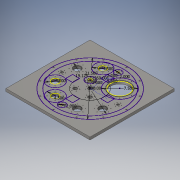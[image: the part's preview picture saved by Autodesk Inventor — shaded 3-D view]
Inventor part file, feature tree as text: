
AUTODESK INVENTOR PART (.ipt)
format: ipt  version: 2018 (Build 220112000, 112)  size: 472,064 bytes
history: native  units: in
note: dims shown in document units (in); Inventor stores cm internally (conversion verified against a paired STEP export)
features: sketch x23, extrude x13, hole x7, pattern_circular x5
ambient origin geometry x8: Origin, YZ Plane, XZ Plane, XY Plane, X Axis, Y Axis, Z Axis, Center Point
bodies: Solid1 (feature_tree)
feature tree (48):
  extrude  "Extrusion1"  Depth=24.0in
  sketch  "Sketch23"  dims[d26=0.1in d27=0.0in]
  extrude  "Extrusion2"  Depth=0.75in
  hole  "Hole1"  [1 undecoded]
  extrude  "Extrusion3"  Depth=1.0in TaperAngle=0.0deg
  extrude  "Extrusion4"  TaperAngle=0.0deg  [1 undecoded]
  hole  "Hole2"  [1 undecoded]
  pattern_circular  "Circular Pattern1"  Count=8 Angle=360.0deg
  extrude  "Extrusion5"  Depth=0.25in
  extrude  "Extrusion6"  Depth=1.04in
  hole  "Hole3"  [1 undecoded]
  pattern_circular  "Circular Pattern5"  Count=6 Angle=360.0deg
  extrude  "Extrusion16"  Depth=0.25in TaperAngle=180.0deg
  extrude  "Extrusion17"  Depth=19.125in
  hole  "Hole9"  [1 undecoded]
  pattern_circular  "Circular Pattern6"  Angle=270.0deg  [1 undecoded]
  sketch  "Sketch29"  dims[d37=0.156in d38=0.38in d39=0.375in d40=0.25in d41=0.5635in d42=0.536in d43=0.8108in d44=3.0in]
  extrude  "Extrusion18"  Depth=0.125in
  extrude  "Extrusion19"  Depth=0.1in TaperAngle=0.0deg
  hole  "Hole10"  [1 undecoded]
  sketch  "Sketch25"  dims[d28=1.9in]
  pattern_circular  "Circular Pattern7"  [2 undecoded]
  extrude  "Extrusion20"  Depth=0.75in
  extrude  "Extrusion21"  TaperAngle=180.0deg  [1 undecoded]
  hole  "Hole11"  [1 undecoded]
  hole  "Hole13"  [1 undecoded]
  pattern_circular  "Circular Pattern9"  [2 undecoded]
  extrude  "Extrusion22"  Depth=0.125in
  sketch  "Sketch1"  dims[d0=24.0in d1=24.0in]
  sketch  "Sketch2"  dims[d2=0.75in d3=0.0in d4=6.0in]
  sketch  "Sketch3"  dims[d5=45.0deg d6=9.35in]
  sketch  "Sketch4"  dims[d7=5.25in d8=1.0in d9=0.0in]
  sketch  "Sketch5"  dims[d10=3.4in d11=0.0in]
  sketch  "Sketch6"  dims[d12=3.1496in d14=360.0deg]
  sketch  "Sketch7"  dims[d16=0.196in d17=0.4in d18=0.375in d19=0.25in d20=0.5635in d21=0.6in d22=0.8108in d23=7.5in]
  sketch  "Sketch8"  dims[d24=1.4086in]
  sketch  "Sketch9"  dims[d25=2.07in]
  sketch  "Sketch26"  dims[d29=0.1in d30=0.0in]
  sketch  "Sketch27"  dims[d31=1.625in]
  sketch  "Sketch28"  dims[d32=0.0in d33=3.1496in d35=360.0deg]
  sketch  "Sketch30"  dims[d45=135.0deg d46=1.04in]
  sketch  "Sketch31"  dims[d47=0.1in d48=0.0in d49=0.9in]
  sketch  "Sketch32"  dims[d50=0.1in d51=0.0in]
  sketch  "Sketch33"  dims[d52=0.945in]
  sketch  "Sketch34"  dims[d53=0.0in d54=2.3622in d56=360.0deg]
  sketch  "Sketch35"  dims[d58=0.156in d59=0.38in d60=0.375in d61=0.25in d62=0.5635in d63=0.536in d64=0.8108in d134=1.1811in d135=180.0deg]
  sketch  "Sketch37"  dims[d167=21.5in d168=19.125in]
  sketch  "Sketch38"  dims[d181=1.1811in d182=180.0deg d185=8.0in d186=270.0deg d187=0.68in d188=0.1in d189=0.0in d190=0.5in d191=0.12in d192=0.0in d193=0.75in d194=180.0deg d195=0.156in d196=0.38in d197=0.375in d198=0.25in d199=0.5635in d200=0.536in d201=0.8108in d202=2.3622in d204=360.0deg d206=4.5in d207=7.5in d208=2.5in d209=2.0in d210=1.5748in d211=270.0deg d213=5.0in d214=90.0deg d215=2.0in d216=2.0in d217=1.5748in d219=360.0deg d221=7.5in d222=0.7902in d223=2.07in d224=0.1in d225=0.0in d226=1.9in d227=0.1in d228=0.0in d229=1.625in d230=3.1496in d232=360.0deg d234=0.156in d235=0.38in d236=0.375in d237=0.25in d238=0.5635in d239=0.536in d240=0.8108in d241=4.5in d242=1.1811in d243=180.0deg d245=2.0in d246=4.5in d247=1.04in d248=0.1in d249=0.0in d250=0.9in d251=0.1in d252=0.0in d253=0.945in d254=2.3622in d256=360.0deg d258=0.156in d259=0.38in d260=0.375in d261=0.25in d262=0.5635in d263=0.536in d264=0.8108in d277=10.4in d278=0.354in d279=0.63in d280=0.375in d281=0.25in d282=0.5635in d283=0.831in d284=0.8108in d285=4.7244in d286=360.0deg d288=5.6in d289=5.85in d290=0.125in d291=0.0in]
note: 14 required parameter values undecoded (feature->parameter linkage not recoverable at this tier; creation-order binding heuristic only, values carry confidence <= 0.55)
